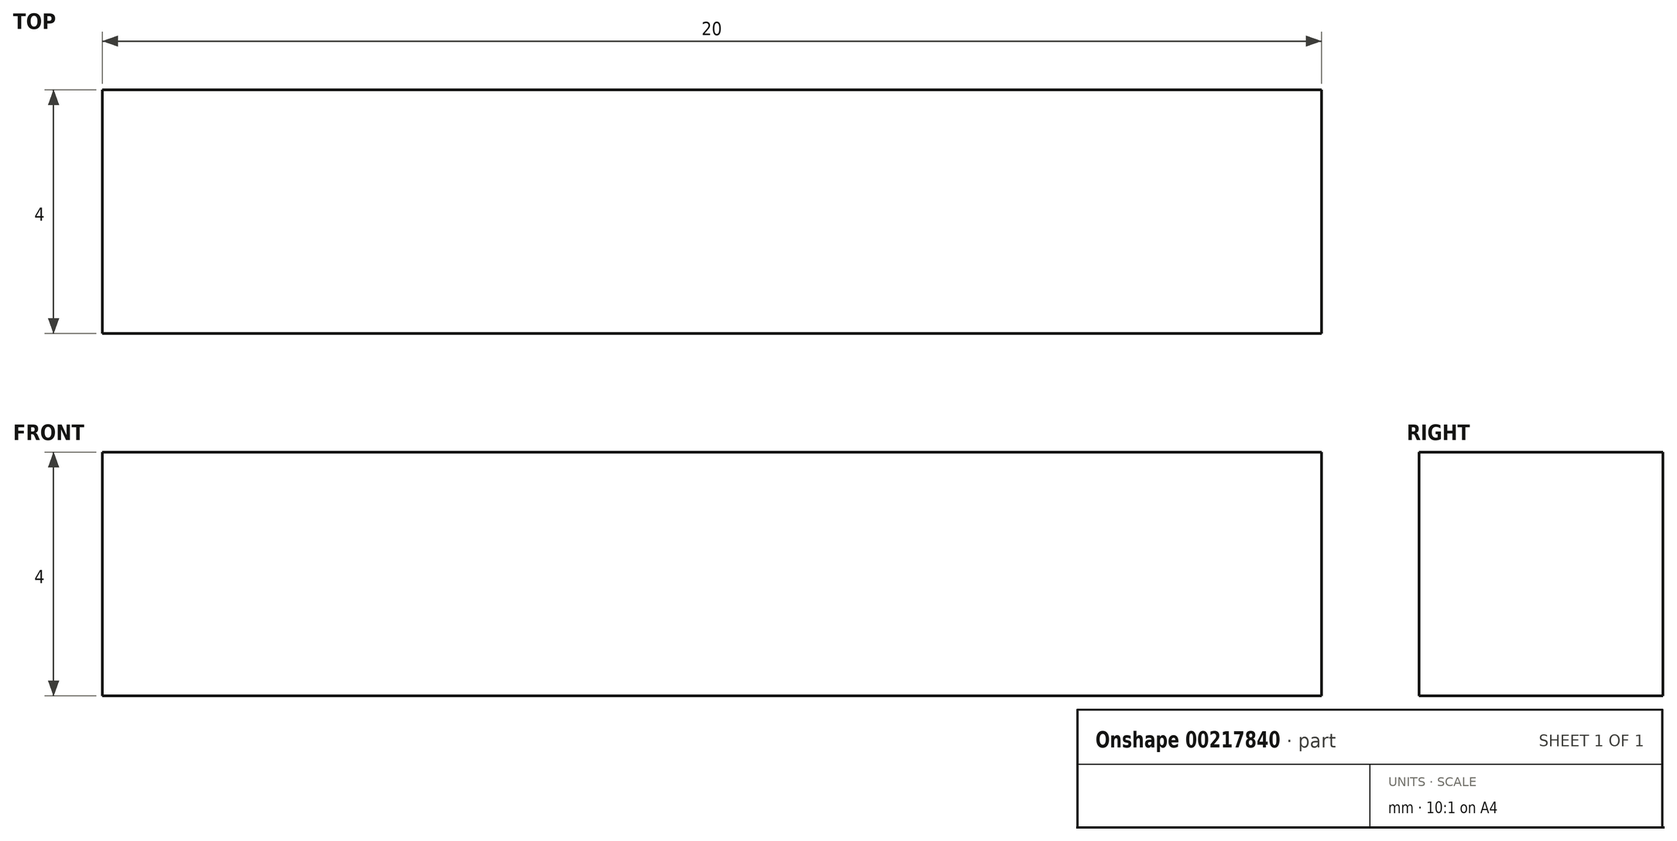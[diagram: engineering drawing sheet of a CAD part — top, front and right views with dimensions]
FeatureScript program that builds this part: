
annotation { "Feature Type Name" : "Feature", "Feature Type Description" : "" }
export const myFeature = defineFeature(function(context is Context, id is Id, definition is map)
    precondition{}
    {
        {
            var Q0;
            Q0=qCreatedBy(makeId("Front.planeOp"),FACE);
            var sketch = newSketch(context, id + "F0", { "sketchPlane" : qUnion([Q0])});
            skLineSegment(sketch, "E0.bottom", {"start": v(0, 0) * mm, "end": v(-20, 0) * mm});
            skLineSegment(sketch, "E0.top", {"start": v(0, -4) * mm, "end": v(-20, -4) * mm});
            skLineSegment(sketch, "E0.left", {"start": v(0, 0) * mm, "end": v(0, -4) * mm});
            skLineSegment(sketch, "E0.right", {"start": v(-20, 0) * mm, "end": v(-20, -4) * mm});
            skSolve(sketch);
        }
        {
            var Q0;
            Q0=makeQuery(id+"F0.imprint","IMPRINT",FACE,{"disambiguationData":[TD([[makeQuery(id+"F0.imprint","IMPRINT",EDGE,{"derivedFrom":sQuery(id+"F0.wireOp",EDGE,"E0.bottom")}),1.0]])]});
            extrude(context, id + "F1", {"entities" : qUnion([Q0]), "depth" : 4 * mm});
        }
    });
